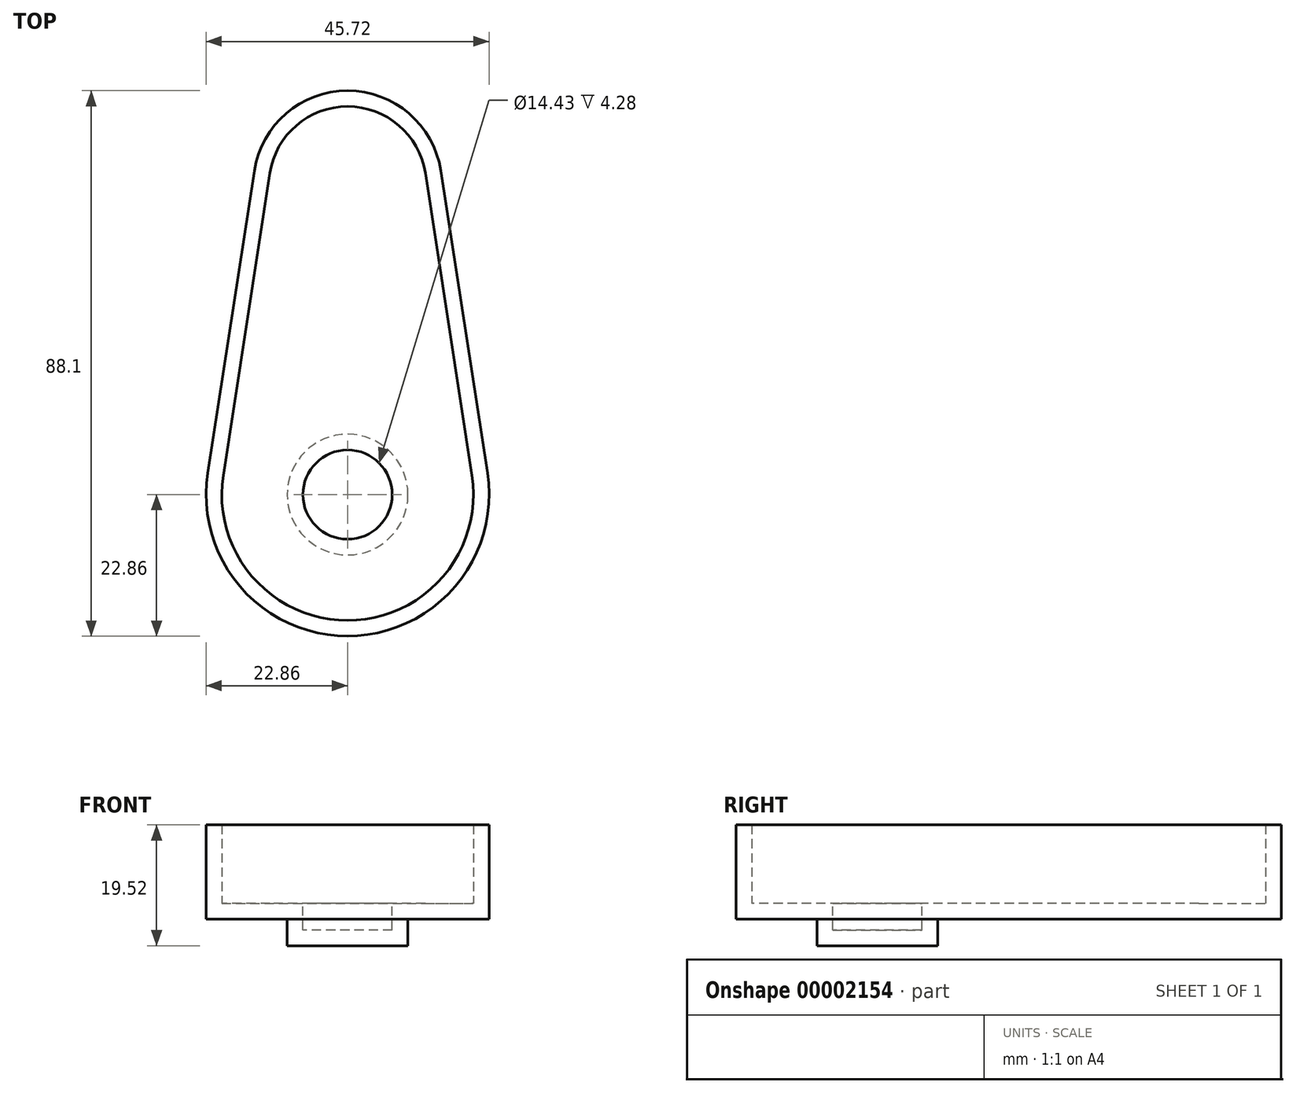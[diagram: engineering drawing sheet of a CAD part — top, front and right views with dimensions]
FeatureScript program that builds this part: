
annotation { "Feature Type Name" : "Feature", "Feature Type Description" : "" }
export const myFeature = defineFeature(function(context is Context, id is Id, definition is map)
    precondition{}
    {
        {
            var Q0;
            Q0=qCreatedBy(makeId("Top.planeOp"),FACE);
            var sketch = newSketch(context, id + "F0", { "sketchPlane" : qUnion([Q0])});
            skCircle(sketch, "E0", {"center": v(0, 0) * mm, "radius": 22.86 * mm, "construction": true});
            skCircle(sketch, "E1", {"center": v(0, 50) * mm, "radius": 15.24 * mm, "construction": true});
            skLineSegment(sketch, "E2", {"start": v(-15.06, 52.32) * mm, "end": v(-22.6, 3.48) * mm});
            skLineSegment(sketch, "E3", {"start": v(15.06, 52.32) * mm, "end": v(22.6, 3.48) * mm});
            skArc(sketch, "E4", {"start": v(-15.06, 52.32) * mm, "mid": v(0, 65.24) * mm, "end": v(15.06, 52.32) * mm});
            skArc(sketch, "E5", {"start": v(22.6, 3.48) * mm, "mid": v(0, -22.86) * mm, "end": v(-22.6, 3.48) * mm});
            skSolve(sketch);
        }
        {
            var Q0;
            Q0 = qSketchRegion(id + "F0", true);
            extrude(context, id + "F1", {"entities" : qUnion([Q0]), "depth" : 15.24 * mm});
        }
        {
            var Q0;
            Q0=makeQuery(id+"F1.opExtrude","CAP_FACE",FACE,{"disambiguationData":[OSD([sQuery(id+"F0.wireOp",EDGE,"E2"),sQuery(id+"F0.wireOp",EDGE,"E3"),sQuery(id+"F0.wireOp",EDGE,"E4"),sQuery(id+"F0.wireOp",EDGE,"E5")])],"isStart":false});
            var sketch = newSketch(context, id + "F2", { "sketchPlane" : qUnion([Q0])});
            skCircle(sketch, "E6", {"center": v(0, 0) * mm, "radius": 9.75 * mm});
            skSolve(sketch);
        }
        {
            var Q0;
            Q0 = qSketchRegion(id + "F2", true);
            var Q1;
            Q1=makeQuery(id+"F1.opExtrude","CAP_FACE",FACE,{"disambiguationData":[OSD([sQuery(id+"F0.wireOp",EDGE,"E2"),sQuery(id+"F0.wireOp",EDGE,"E3"),sQuery(id+"F0.wireOp",EDGE,"E4"),sQuery(id+"F0.wireOp",EDGE,"E5")])],"isStart":true});
            extrude(context, id + "F3", {"entities" : qUnion([Q0]), "operationType" : NewBodyOperationType.ADD, "oppositeDirection" : true, "endBoundEntity" : qUnion([Q1]), "depth" : 19.52 * mm});
        }
        {
            var Q0;
            Q0=makeQuery(id+"F1.opExtrude","CAP_FACE",FACE,{"disambiguationData":[OSD([sQuery(id+"F0.wireOp",EDGE,"E2"),sQuery(id+"F0.wireOp",EDGE,"E3"),sQuery(id+"F0.wireOp",EDGE,"E4"),sQuery(id+"F0.wireOp",EDGE,"E5")])],"isStart":false});
            shell(context, id + "F4", {"entities" : qUnion([Q0]), "thickness" : 2.54 * mm});
        }
    });
